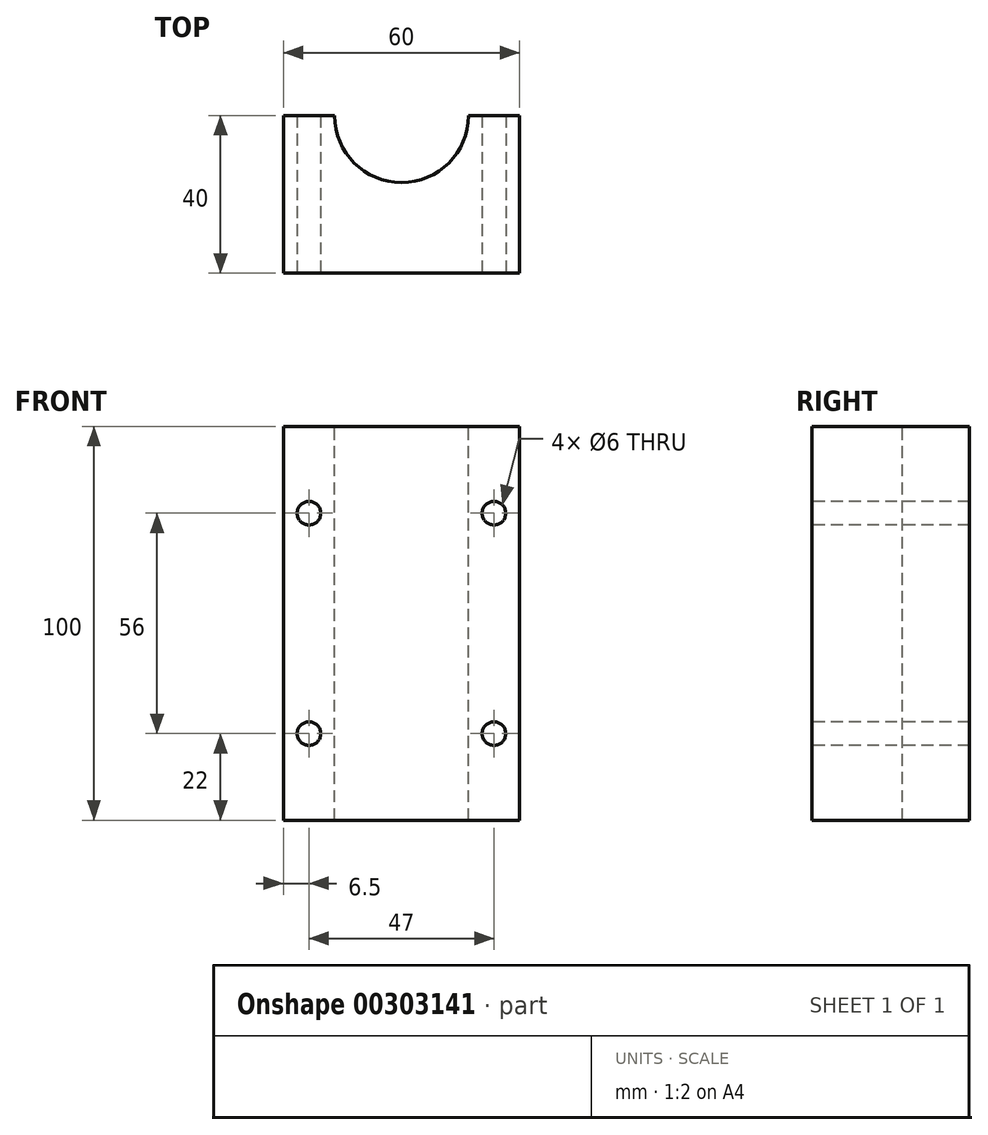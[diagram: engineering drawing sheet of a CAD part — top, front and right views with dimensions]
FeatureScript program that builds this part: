
annotation { "Feature Type Name" : "Feature", "Feature Type Description" : "" }
export const myFeature = defineFeature(function(context is Context, id is Id, definition is map)
    precondition{}
    {
        {
            var Q0;
            Q0=qCreatedBy(makeId("Top.planeOp"),FACE);
            var sketch = newSketch(context, id + "F0", { "sketchPlane" : qUnion([Q0])});
            skLineSegment(sketch, "E0.bottom", {"start": v(-30, 0) * mm, "end": v(30, 0) * mm});
            skLineSegment(sketch, "E0.top", {"start": v(-30, -40) * mm, "end": v(30, -40) * mm});
            skLineSegment(sketch, "E0.left", {"start": v(-30, 0) * mm, "end": v(-30, -40) * mm});
            skLineSegment(sketch, "E0.right", {"start": v(30, 0) * mm, "end": v(30, -40) * mm});
            skLineSegment(sketch, "E1", {"start": v(0, 60.06) * mm, "end": v(0, -68.5) * mm, "construction": true});
            skLineSegment(sketch, "E2", {"start": v(-52.55, 0) * mm, "end": v(61, 0) * mm, "construction": true});
            skSolve(sketch);
        }
        {
            var Q0;
            Q0 = qSketchRegion(id + "F0", true);
            extrude(context, id + "F1", {"entities" : qUnion([Q0]), "depth" : 100 * mm});
        }
        {
            var Q0;
            Q0=makeQuery(id+"F1.opExtrude","CAP_FACE",FACE,{"disambiguationData":[OSD([sQuery(id+"F0.wireOp",EDGE,"E0.bottom"),sQuery(id+"F0.wireOp",EDGE,"E0.top"),sQuery(id+"F0.wireOp",EDGE,"E0.left"),sQuery(id+"F0.wireOp",EDGE,"E0.right")])],"isStart":false});
            var sketch = newSketch(context, id + "F2", { "sketchPlane" : qUnion([Q0])});
            skCircle(sketch, "E3", {"center": v(0, 0) * mm, "radius": 17 * mm});
            skSolve(sketch);
        }
        {
            var Q0;
            Q0 = qSketchRegion(id + "F2", true);
            extrude(context, id + "F3", {"entities" : qUnion([Q0]), "operationType" : NewBodyOperationType.REMOVE, "oppositeDirection" : true, "depth" : 100 * mm});
        }
        {
            var Q0;
            Q0=makeQuery(id+"F1.opExtrude","SWEPT_FACE",FACE,{"disambiguationData":[OSD([sQuery(id+"F0.wireOp",EDGE,"E0.top")])]});
            var sketch = newSketch(context, id + "F4", { "sketchPlane" : qUnion([Q0])});
            skLineSegment(sketch, "E4", {"start": v(0, -13.95) * mm, "end": v(0, 111.64) * mm, "construction": true});
            skPoint(sketch, "E4.endSnap0", {"position": v(0, 100) * mm});
            skLineSegment(sketch, "E5", {"start": v(44.42, 100) * mm, "end": v(-52.5, 100) * mm, "construction": true});
            skLineSegment(sketch, "E6", {"start": v(-30, 113.66) * mm, "end": v(-30, -23.44) * mm, "construction": true});
            skLineSegment(sketch, "E7", {"start": v(-52.5, 0) * mm, "end": v(48.46, 0) * mm, "construction": true});
            skLineSegment(sketch, "E8", {"start": v(30, 114.88) * mm, "end": v(30, -19.8) * mm, "construction": true});
            skCircle(sketch, "E9", {"center": v(-23.5, 78) * mm, "radius": 3 * mm});
            skCircle(sketch, "E10", {"center": v(-23.5, 22) * mm, "radius": 3 * mm});
            skCircle(sketch, "E11", {"center": v(23.5, 22) * mm, "radius": 3 * mm});
            skCircle(sketch, "E12", {"center": v(23.5, 78) * mm, "radius": 3 * mm});
            skSolve(sketch);
        }
        {
            var Q0;
            Q0 = qSketchRegion(id + "F4", true);
            extrude(context, id + "F5", {"entities" : qUnion([Q0]), "operationType" : NewBodyOperationType.REMOVE, "oppositeDirection" : true, "depth" : 45 * mm});
        }
    });
